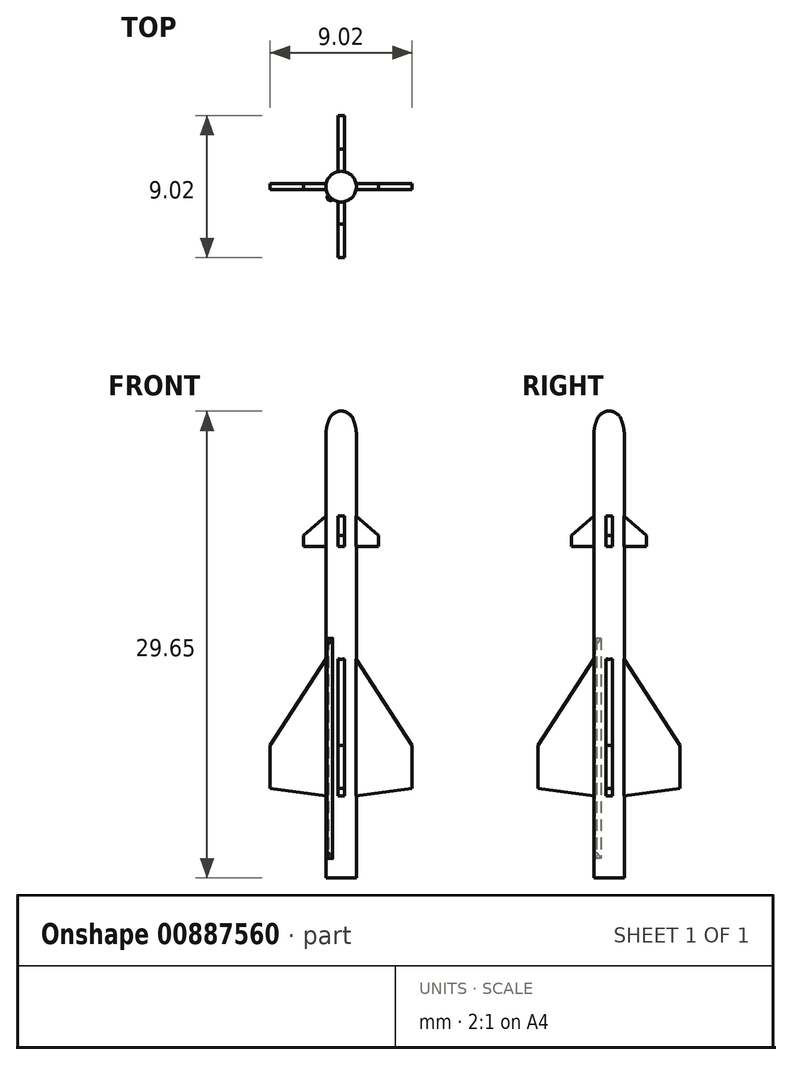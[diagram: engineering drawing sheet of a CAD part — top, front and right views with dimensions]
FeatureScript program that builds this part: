
annotation { "Feature Type Name" : "Feature", "Feature Type Description" : "" }
export const myFeature = defineFeature(function(context is Context, id is Id, definition is map)
    precondition{}
    {
        {
            var Q0;
            Q0=qCreatedBy(makeId("Front.planeOp"),FACE);
            var sketch = newSketch(context, id + "F0", { "sketchPlane" : qUnion([Q0])});
            skLineSegment(sketch, "E0", {"start": v(0, 0) * mm, "end": v(0, 29.65) * mm});
            skLineSegment(sketch, "E1", {"start": v(0.97, 28.06) * mm, "end": v(0.97, 0) * mm});
            skLineSegment(sketch, "E2", {"start": v(0.97, 0) * mm, "end": v(0, 0) * mm});
            skArc(sketch, "E3", {"start": v(0.77, 29.13) * mm, "mid": v(0.46, 29.51) * mm, "end": v(0, 29.65) * mm});
            skArc(sketch, "E4", {"start": v(0.97, 28.06) * mm, "mid": v(0.92, 28.6) * mm, "end": v(0.77, 29.13) * mm});
            skLineSegment(sketch, "E5", {"start": v(0, 29.65) * mm, "end": v(709.8, 29.65) * mm, "construction": true});
            skSolve(sketch);
        }
        {
            var Q0;
            Q0=makeQuery(id+"F0.imprint","IMPRINT",FACE,{"disambiguationData":[TD([[makeQuery(id+"F0.imprint","IMPRINT",EDGE,{"derivedFrom":sQuery(id+"F0.wireOp",EDGE,"E0")}),-1.0]])]});
            var Q1;
            Q1=sQuery(id+"F0.wireOp",EDGE,"E0");
            revolve(context, id + "F1", {"surfaceOperationType" : NewSurfaceOperationType.NEW, "entities" : qUnion([Q0]), "axis" : qUnion([Q1]), "revolveType" : RevolveType.FULL});
        }
        {
            var Q0;
            Q0=qCreatedBy(makeId("Front.planeOp"),FACE);
            var sketch = newSketch(context, id + "F2", { "sketchPlane" : qUnion([Q0])});
            skLineSegment(sketch, "E6.0", {"start": v(0.97, 28.06) * mm, "end": v(-0.97, 28.06) * mm, "construction": true});
            skLineSegment(sketch, "E7", {"start": v(0, 5.07) * mm, "end": v(4.51, 5.7) * mm});
            skLineSegment(sketch, "E8", {"start": v(4.51, 5.7) * mm, "end": v(4.51, 8.4) * mm});
            skLineSegment(sketch, "E9", {"start": v(4.51, 8.4) * mm, "end": v(0.97, 13.89) * mm});
            skLineSegment(sketch, "E10", {"start": v(0.4, 14.78) * mm, "end": v(0.4, 21.04) * mm});
            skLineSegment(sketch, "E11", {"start": v(0.4, 21.04) * mm, "end": v(2.38, 21.04) * mm});
            skLineSegment(sketch, "E12", {"start": v(2.38, 21.04) * mm, "end": v(2.38, 21.74) * mm});
            skLineSegment(sketch, "E13", {"start": v(2.37, 21.74) * mm, "end": v(0, 23.85) * mm});
            skLineSegment(sketch, "E14", {"start": v(0, 23.85) * mm, "end": v(0, 5.07) * mm});
            skLineSegment(sketch, "E15", {"start": v(0.97, 28.06) * mm, "end": v(0.97, 0) * mm, "construction": true});
            skPoint(sketch, "E16", {"position": v(0.97, 5.2) * mm});
            skPoint(sketch, "E17", {"position": v(0.97, 22.99) * mm});
            skLineSegment(sketch, "E18", {"start": v(0.97, 13.89) * mm, "end": v(0.4, 14.78) * mm});
            skSolve(sketch);
        }
        {
            var Q0;
            Q0=qSketchRegion(id+"F2",true);
            extrude(context, id + "F3", {"entities" : qUnion([Q0]), "operationType" : NewBodyOperationType.ADD, "oppositeDirection" : true, "depth" : .4 * mm, "offsetDistance" : 25 * mm, "symmetric" : true});
        }
        {
            var Q0;
            Q0=makeQuery(id+"F1.opRevolve","SWEPT_BODY",BODY,{"disambiguationData":[OSD([sQuery(id+"F0.wireOp",EDGE,"E0"),sQuery(id+"F0.wireOp",EDGE,"E1"),sQuery(id+"F0.wireOp",EDGE,"E2"),sQuery(id+"F0.wireOp",EDGE,"h1jDSi8t-veb7-85qg-XgDk-6E8DmZjBuz4r")])]});
            var Q1;
            Q1=makeQuery(id+"F1.opRevolve","SWEPT_FACE",FACE,{"disambiguationData":[OSD([sQuery(id+"F0.wireOp",EDGE,"E1")])]});
            circularPattern(context, id + "F4", {"operationType" : NewBodyOperationType.ADD, "entities" : qUnion([Q0]), "axis" : qUnion([Q1]), "angle" : 360 * degree, "instanceCount" : 4, "equalSpace" : true, "computeTransformsWithoutBuiltin" : true});
        }
        {
            var Q0;
            Q0=qCreatedBy(makeId("Top.planeOp"),FACE);
            cPlane(context, id + "F5", {"entities" : qUnion([Q0]), "cplaneType" : CPlaneType.OFFSET, "offset" : (240 / 144) * mm, "width" : 150 * mm, "height" : 150 * mm});
        }
        {
            var Q0;
            Q0=qCreatedBy(id+"F5.planeOp",FACE);
            var sketch = newSketch(context, id + "F6", { "sketchPlane" : qUnion([Q0])});
            skLineSegment(sketch, "E19", {"start": v(-0.83, -0.55) * mm, "end": v(-0.63, -0.35) * mm});
            skLineSegment(sketch, "E20", {"start": v(-0.63, -0.35) * mm, "end": v(-0.35, -0.63) * mm});
            skLineSegment(sketch, "E21", {"start": v(-0.35, -0.63) * mm, "end": v(-0.55, -0.83) * mm});
            skArc(sketch, "E22", {"start": v(-0.83, -0.55) * mm, "mid": v(-0.83, -0.83) * mm, "end": v(-0.55, -0.83) * mm});
            skLineSegment(sketch, "E23", {"start": v(-0.5, -0.5) * mm, "end": v(0, 0) * mm, "construction": true});
            skLineSegment(sketch, "E24", {"start": v(0, 0) * mm, "end": v(-0.48, 0) * mm, "construction": true});
            skSolve(sketch);
        }
        {
            var Q0;
            Q0=makeQuery(id+"F6.imprint","IMPRINT",FACE,{"disambiguationData":[TD([[makeQuery(id+"F6.imprint","IMPRINT",EDGE,{"derivedFrom":sQuery(id+"F6.wireOp",EDGE,"E19")}),-1.0]])]});
            extrude(context, id + "F7", {"entities" : qUnion([Q0]), "operationType" : NewBodyOperationType.ADD, "depth" : (1890 / 144) * mm, "offsetDistance" : 25 * mm});
        }
        {
            var Q0;
            Q0=makeQuery(id+"F7.boolean.opBoolean","INTERSECT",EDGE,{"derivedFrom":[makeQuery(id+"F1.opRevolve","SWEPT_FACE",FACE,{"disambiguationData":[OSD([sQuery(id+"F0.wireOp",EDGE,"E1")])]}),makeQuery(id+"F7.opExtrude","CAP_FACE",FACE,{"disambiguationData":[OSD([sQuery(id+"F6.wireOp",EDGE,"E19"),sQuery(id+"F6.wireOp",EDGE,"E20"),sQuery(id+"F6.wireOp",EDGE,"E21"),sQuery(id+"F6.wireOp",EDGE,"E22")])],"isStart":false})]});
            var Q1;
            Q1=makeQuery(id+"F7.boolean.opBoolean","INTERSECT",EDGE,{"derivedFrom":[makeQuery(id+"F1.opRevolve","SWEPT_FACE",FACE,{"disambiguationData":[OSD([sQuery(id+"F0.wireOp",EDGE,"E1")])]}),makeQuery(id+"F7.opExtrude","CAP_FACE",FACE,{"disambiguationData":[OSD([sQuery(id+"F6.wireOp",EDGE,"E19"),sQuery(id+"F6.wireOp",EDGE,"E20"),sQuery(id+"F6.wireOp",EDGE,"E21"),sQuery(id+"F6.wireOp",EDGE,"E22")])],"isStart":true})]});
            chamfer(context, id + "F8", {"entities" : qUnion([Q0, Q1]), "chamferType" : ChamferType.OFFSET_ANGLE, "width" : .25 * mm, "oppositeDirection" : true, "angle" : 60 * degree, "tangentPropagation" : true});
        }
    });
